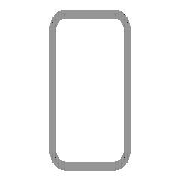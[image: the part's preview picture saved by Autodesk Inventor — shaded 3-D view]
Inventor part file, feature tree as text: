
AUTODESK INVENTOR PART (.ipt)
format: ipt  version: 2025 (Build 290162010, 162A)  size: 150,016 bytes
history: native  units: mm (DEFAULTED — no unit token found)
features: other x4, plane x3, split x2, sketch x1
ambient origin geometry x8: Origin, YZ Plane, XZ Plane, XY Plane, X Axis, Y Axis, Z Axis, Center Point
bodies: Solid1 (feature_tree), Body (feature_tree)
feature tree (10):
  parser-record x1  (decoder bookkeeping rows leaked as tree rows — omitted from the tree; the rows remain in map.json)
  other  "Driven Length"
  other  "Start Plane"
  other  "End Plane"
  plane  "Work Plane4"
  split  "Split1"
  plane  "Work Plane5"
  split  "Split2"
  sketch  "Sketch3"  dims[d3=615.253612mm d4=0.0mm d7=4.0mm d9=20.0mm d11=40.0mm d12=2.0mm d13=17.365243mm d14=632.618856mm d15=10.0mm d16=20.0mm d17=90.0deg d18=615.253612mm]
  plane  "Work Plane3"
